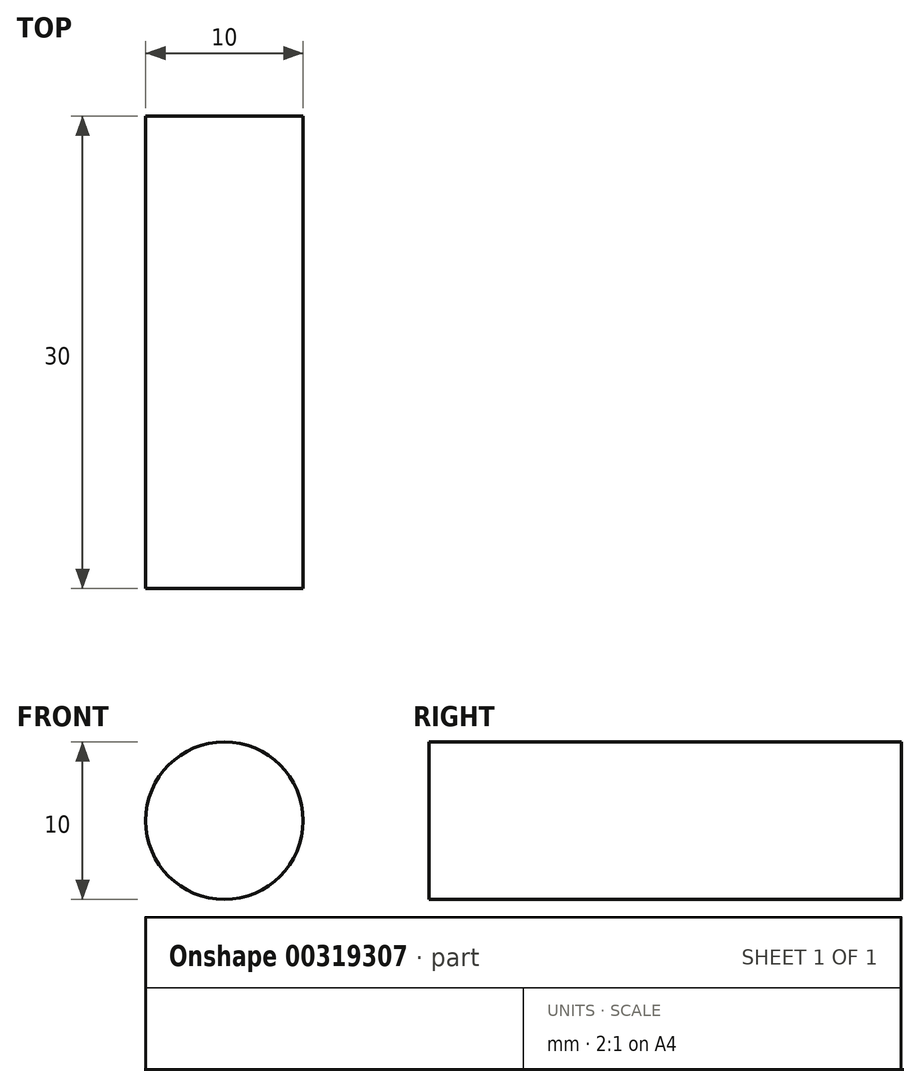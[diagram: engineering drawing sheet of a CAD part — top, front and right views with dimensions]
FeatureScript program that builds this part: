
annotation { "Feature Type Name" : "Feature", "Feature Type Description" : "" }
export const myFeature = defineFeature(function(context is Context, id is Id, definition is map)
    precondition{}
    {
        {
            var Q0;
            Q0=qCreatedBy(makeId("Front.planeOp"),FACE);
            var sketch = newSketch(context, id + "F0", { "sketchPlane" : qUnion([Q0])});
            skCircle(sketch, "E0", {"center": v(0, 0) * mm, "radius": 5 * mm});
            skSolve(sketch);
        }
        {
            var Q0;
            Q0 = qSketchRegion(id + "F0", true);
            extrude(context, id + "F1", {"entities" : qUnion([Q0]), "depth" : 30 * mm});
        }
    });
